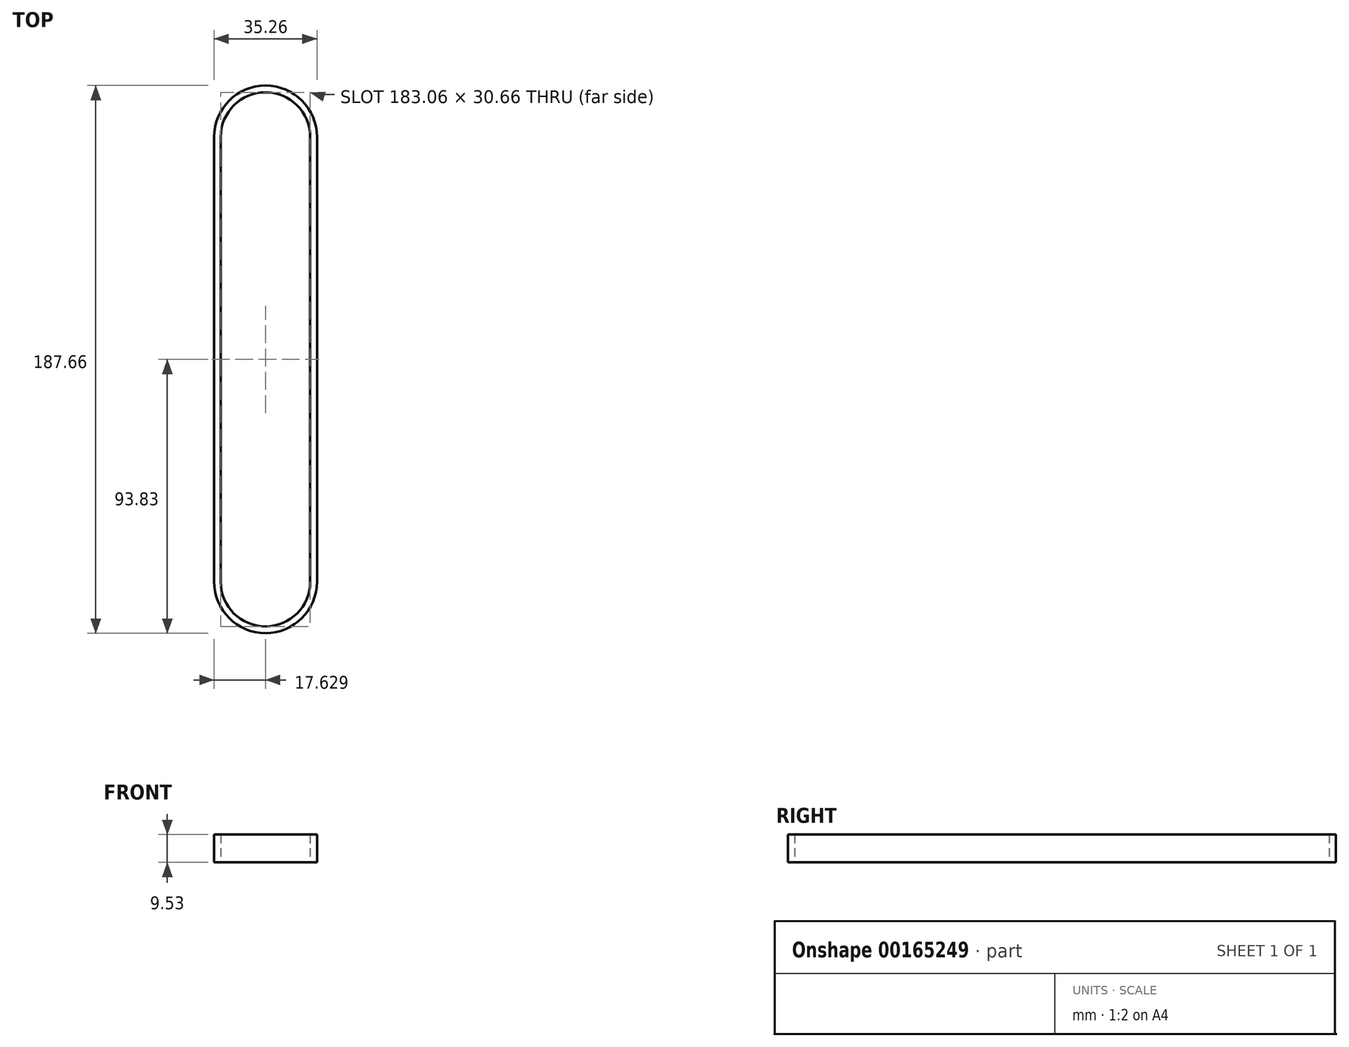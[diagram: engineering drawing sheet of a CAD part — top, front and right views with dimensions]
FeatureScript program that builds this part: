
annotation { "Feature Type Name" : "Feature", "Feature Type Description" : "" }
export const myFeature = defineFeature(function(context is Context, id is Id, definition is map)
    precondition{}
    {
        {
            var Q0;
            Q0=qCreatedBy(makeId("Top.planeOp"),FACE);
            var sketch = newSketch(context, id + "F0", { "sketchPlane" : qUnion([Q0])});
            skLineSegment(sketch, "E0.bottom", {"start": v(0, 0) * mm, "end": v(30.66, 0) * mm, "construction": true});
            skLineSegment(sketch, "E0.top", {"start": v(0, 152.4) * mm, "end": v(30.66, 152.4) * mm, "construction": true});
            skLineSegment(sketch, "E0.left", {"start": v(0, 0) * mm, "end": v(0, 152.4) * mm});
            skLineSegment(sketch, "E0.right", {"start": v(30.66, 0) * mm, "end": v(30.66, 152.4) * mm});
            skArc(sketch, "E1", {"start": v(30.66, 152.4) * mm, "mid": v(15.33, 167.73) * mm, "end": v(0, 152.4) * mm});
            skArc(sketch, "E2", {"start": v(0, 0) * mm, "mid": v(15.33, -15.33) * mm, "end": v(30.66, 0) * mm});
            skLineSegment(sketch, "E3", {"start": v(0, 152.4) * mm, "end": v(-2.3, 152.4) * mm, "construction": true});
            skLineSegment(sketch, "E4", {"start": v(30.66, 152.4) * mm, "end": v(32.96, 152.4) * mm, "construction": true});
            skLineSegment(sketch, "E5", {"start": v(32.96, 152.4) * mm, "end": v(32.96, 0) * mm});
            skLineSegment(sketch, "E6", {"start": v(32.96, 0) * mm, "end": v(30.66, 0) * mm, "construction": true});
            skLineSegment(sketch, "E7", {"start": v(0, 0) * mm, "end": v(-2.3, 0) * mm});
            skLineSegment(sketch, "E8", {"start": v(-2.3, 0) * mm, "end": v(-2.3, 152.4) * mm});
            skArc(sketch, "E9", {"start": v(-2.3, 0) * mm, "mid": v(15.33, -17.63) * mm, "end": v(32.96, 0) * mm});
            skArc(sketch, "E10", {"start": v(32.96, 152.4) * mm, "mid": v(15.33, 170.03) * mm, "end": v(-2.3, 152.4) * mm});
            skSolve(sketch);
        }
        {
            var Q0;
            Q0 = qSketchRegion(id + "F0", true);
            extrude(context, id + "F1", {"entities" : qUnion([Q0]), "depth" : 9.52 * mm});
        }
    });
